# Revit family: Plumbing_Sloan_Sink_EHS-1000p
name_source: partatom
category: Plumbing Fixtures
units: mm (PartAtom-declared; Revit-internal decimal feet)

## family parameters
Cut with Voids When Loaded = No
Host = Face
OmniClass Number = 23.45.05.14.14
OmniClass Title = Sinks/Lavatories
Part Type = Normal
Room Calculation Point = No
Round Connector Dimension = Use Diameter
Shared = No

## types (1)
- EHS-1000
    Actual Water Flow = 0.0 GPM
    Apparent Load = 1650 VA
    Assembly Code = D2010400
    CW Connection = No
    Current = 15 A
    Default Elevation = 32"
    Depth = 16"
    Description = Stainless Steel 1-Station Wall-Mounted Handwashing Sink.
    Drain Flow = 0.0 GPM
    Drain Pipe Diameter = 1 1/2"
    Frequency = 60 Hz
    HW Connection = No
    Height = 23"
    Keynote = 10000
    Manufacturer = Sloan Valve
    Model = EHS-1000
    Number of Poles = 1
    Power Factor = 1
    Product Material = Sloan - Metal - Stainless Steel 304
    Product data url = https://bimobject.com
    URL = https://www.sloan.com
    Vent Connection = No
    Voltage = 110 V
    Waste Connection = Yes
    Width = 19"

## geometry (parser evidence)
native form markers: Sweep x2
no freeform markers — native parametric forms only
